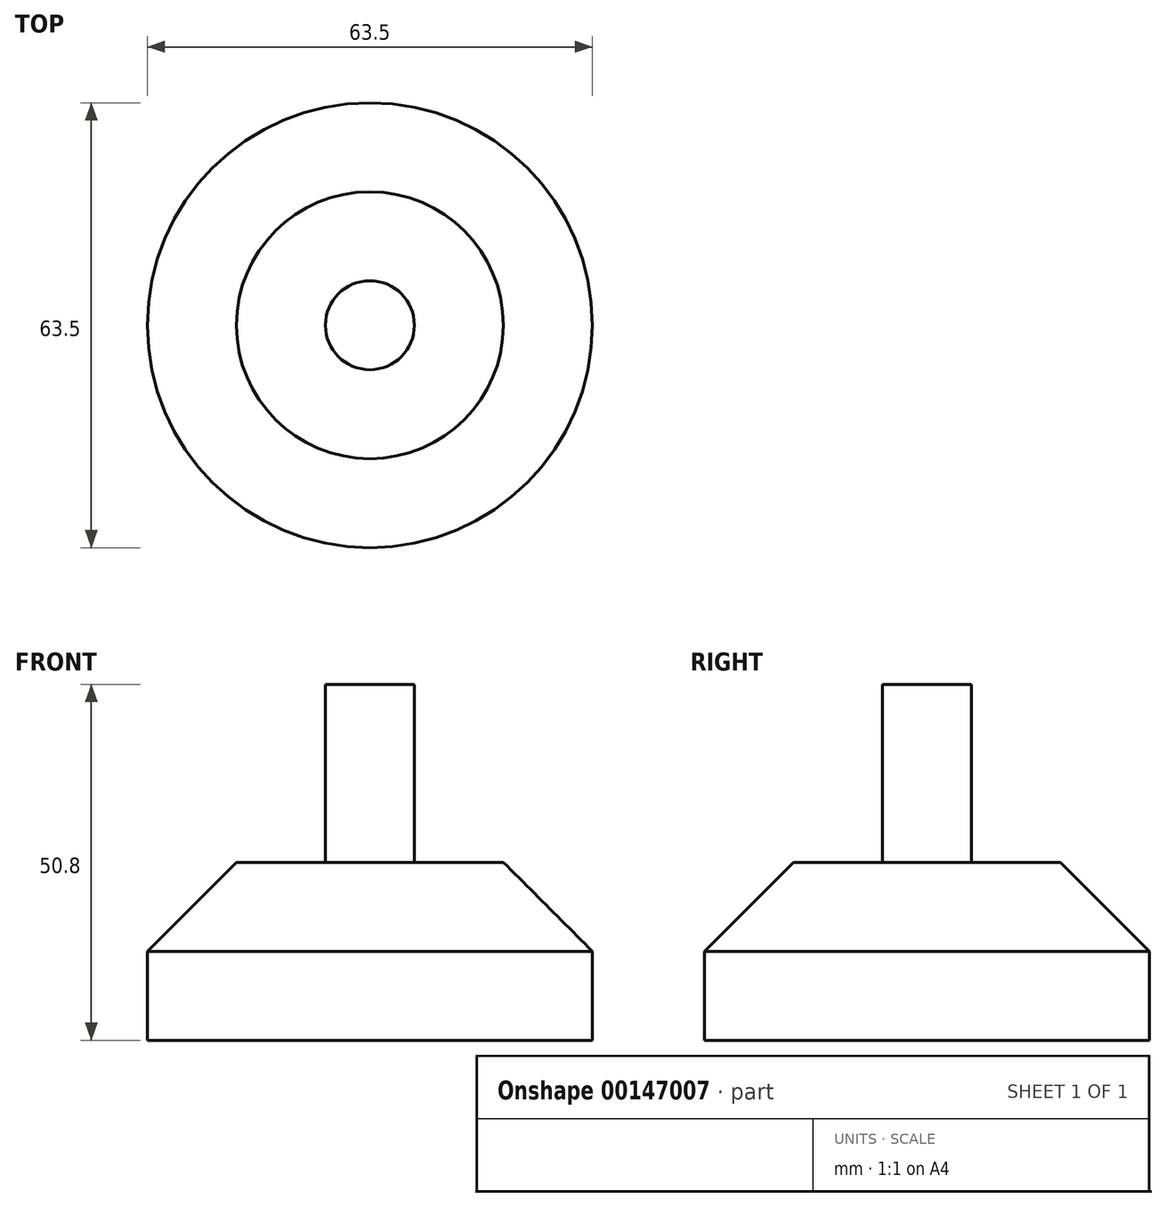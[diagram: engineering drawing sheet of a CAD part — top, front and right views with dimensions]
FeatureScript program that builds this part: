
annotation { "Feature Type Name" : "Feature", "Feature Type Description" : "" }
export const myFeature = defineFeature(function(context is Context, id is Id, definition is map)
    precondition{}
    {
        {
            var Q0;
            Q0=qCreatedBy(makeId("Top.planeOp"),FACE);
            var sketch = newSketch(context, id + "F0", { "sketchPlane" : qUnion([Q0])});
            skCircle(sketch, "E0", {"center": v(0, 0) * mm, "radius": 31.75 * mm});
            skSolve(sketch);
        }
        {
            var Q0;
            Q0=makeQuery(id+"F0.imprint","IMPRINT",FACE,{"disambiguationData":[TD([[makeQuery(id+"F0.imprint","IMPRINT",EDGE,{"derivedFrom":sQuery(id+"F0.wireOp",EDGE,"E0")}),1.0]])]});
            var Q1;
            Q1=sQuery(id+"F0.wireOp",EDGE,"E0");
            extrude(context, id + "F1", {"entities" : qUnion([Q0]), "surfaceEntities" : qUnion([Q1]), "depth" : 25.4 * mm});
        }
        {
            var Q0;
            Q0=makeQuery(id+"F1.opExtrude","CAP_EDGE",EDGE,{"disambiguationData":[OSD([sQuery(id+"F0.wireOp",EDGE,"E0")])],"isStart":false});
            chamfer(context, id + "F2", {"entities" : qUnion([Q0]), "width" : 12.7 * mm, "tangentPropagation" : true});
        }
        {
            var Q0;
            Q0=makeQuery(id+"F1.opExtrude","CAP_FACE",FACE,{"disambiguationData":[OSD([sQuery(id+"F0.wireOp",EDGE,"E0")])],"isStart":false});
            var sketch = newSketch(context, id + "F3", { "sketchPlane" : qUnion([Q0])});
            skCircle(sketch, "E1", {"center": v(0, 0) * mm, "radius": 6.35 * mm});
            skSolve(sketch);
        }
        {
            var Q0;
            Q0 = qSketchRegion(id + "F3", true);
            extrude(context, id + "F4", {"entities" : qUnion([Q0]), "operationType" : NewBodyOperationType.ADD, "depth" : 25.4 * mm});
        }
    });
